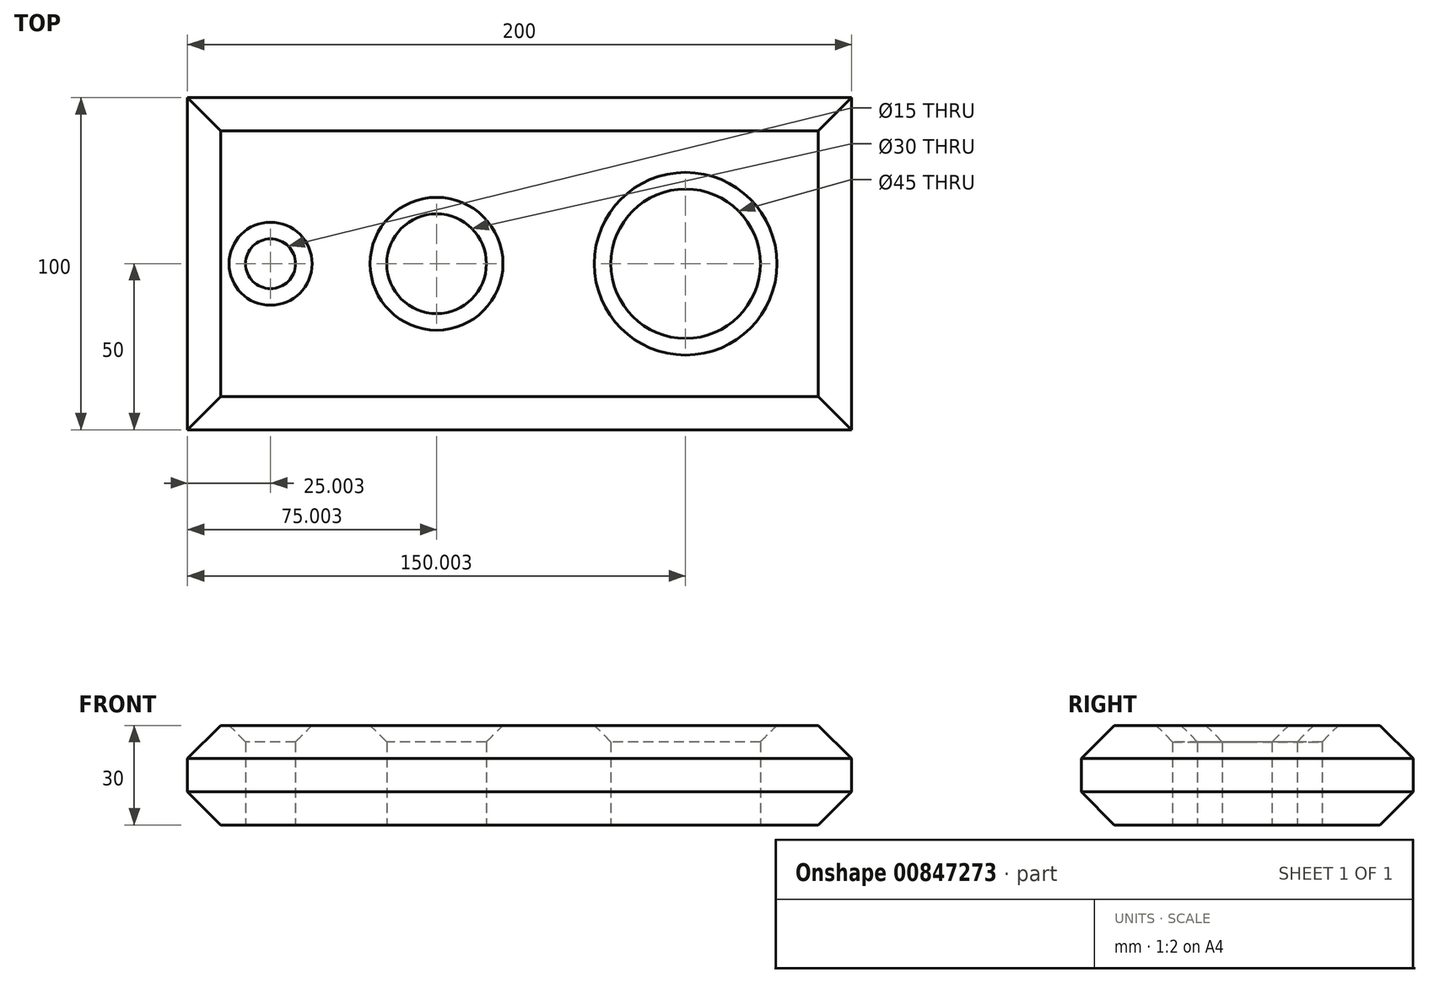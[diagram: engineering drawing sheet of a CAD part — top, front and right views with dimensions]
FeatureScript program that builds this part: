
annotation { "Feature Type Name" : "Feature", "Feature Type Description" : "" }
export const myFeature = defineFeature(function(context is Context, id is Id, definition is map)
    precondition{}
    {
        {
            var Q0;
            Q0=qCreatedBy(makeId("Top.planeOp"),FACE);
            var sketch = newSketch(context, id + "F0", { "sketchPlane" : qUnion([Q0])});
            skLineSegment(sketch, "E0.bottom", {"start": v(-96.1, 50) * mm, "end": v(103.9, 50) * mm});
            skLineSegment(sketch, "E0.top", {"start": v(-96.1, -50) * mm, "end": v(103.9, -50) * mm});
            skLineSegment(sketch, "E0.left", {"start": v(-96.1, 50) * mm, "end": v(-96.1, -50) * mm});
            skLineSegment(sketch, "E0.right", {"start": v(103.9, 50) * mm, "end": v(103.9, -50) * mm});
            skCircle(sketch, "E1", {"center": v(-71.1, 0) * mm, "radius": 7.5 * mm});
            skCircle(sketch, "E2", {"center": v(-21.1, 0) * mm, "radius": 15 * mm});
            skCircle(sketch, "E3", {"center": v(53.9, 0) * mm, "radius": 22.5 * mm});
            skSolve(sketch);
        }
        {
            var Q0;
            Q0 = qSketchRegion(id + "F0", true);
            extrude(context, id + "F1", {"entities" : qUnion([Q0]), "depth" : 30 * mm, "offsetDistance" : 25 * mm});
        }
        {
            var Q0;
            Q0=makeQuery(id+"F1.opExtrude","CAP_EDGE",EDGE,{"disambiguationData":[OSD([sQuery(id+"F0.wireOp",EDGE,"E0.bottom")])],"isStart":false});
            var Q1;
            Q1=makeQuery(id+"F1.opExtrude","CAP_EDGE",EDGE,{"disambiguationData":[OSD([sQuery(id+"F0.wireOp",EDGE,"E0.left")])],"isStart":false});
            var Q2;
            Q2=makeQuery(id+"F1.opExtrude","CAP_EDGE",EDGE,{"disambiguationData":[OSD([sQuery(id+"F0.wireOp",EDGE,"E0.top")])],"isStart":false});
            var Q3;
            Q3=makeQuery(id+"F1.opExtrude","CAP_EDGE",EDGE,{"disambiguationData":[OSD([sQuery(id+"F0.wireOp",EDGE,"E0.right")])],"isStart":false});
            var Q4;
            Q4=makeQuery(id+"F1.opExtrude","CAP_EDGE",EDGE,{"disambiguationData":[OSD([sQuery(id+"F0.wireOp",EDGE,"E0.top")])],"isStart":true});
            var Q5;
            Q5=makeQuery(id+"F1.opExtrude","CAP_EDGE",EDGE,{"disambiguationData":[OSD([sQuery(id+"F0.wireOp",EDGE,"E0.bottom")])],"isStart":true});
            var Q6;
            Q6=makeQuery(id+"F1.opExtrude","CAP_EDGE",EDGE,{"disambiguationData":[OSD([sQuery(id+"F0.wireOp",EDGE,"E0.right")])],"isStart":true});
            var Q7;
            Q7=makeQuery(id+"F1.opExtrude","CAP_EDGE",EDGE,{"disambiguationData":[OSD([sQuery(id+"F0.wireOp",EDGE,"E0.left")])],"isStart":true});
            chamfer(context, id + "F2", {"entities" : qUnion([Q0, Q1, Q2, Q3, Q4, Q5, Q6, Q7]), "chamferType" : ChamferType.OFFSET_ANGLE, "width" : 10 * mm, "oppositeDirection" : false, "angle" : 45 * degree, "tangentPropagation" : true});
        }
        {
            var Q0;
            Q0=makeQuery(id+"F1.opExtrude","CAP_EDGE",EDGE,{"disambiguationData":[OSD([sQuery(id+"F0.wireOp",EDGE,"E1")])],"isStart":false});
            var Q1;
            Q1=makeQuery(id+"F1.opExtrude","CAP_EDGE",EDGE,{"disambiguationData":[OSD([sQuery(id+"F0.wireOp",EDGE,"E2")])],"isStart":false});
            var Q2;
            Q2=makeQuery(id+"F1.opExtrude","CAP_EDGE",EDGE,{"disambiguationData":[OSD([sQuery(id+"F0.wireOp",EDGE,"E3")])],"isStart":false});
            chamfer(context, id + "F3", {"entities" : qUnion([Q0, Q1, Q2]), "chamferType" : ChamferType.OFFSET_ANGLE, "width" : 5 * mm, "oppositeDirection" : false, "angle" : 45 * degree, "tangentPropagation" : true});
        }
    });
